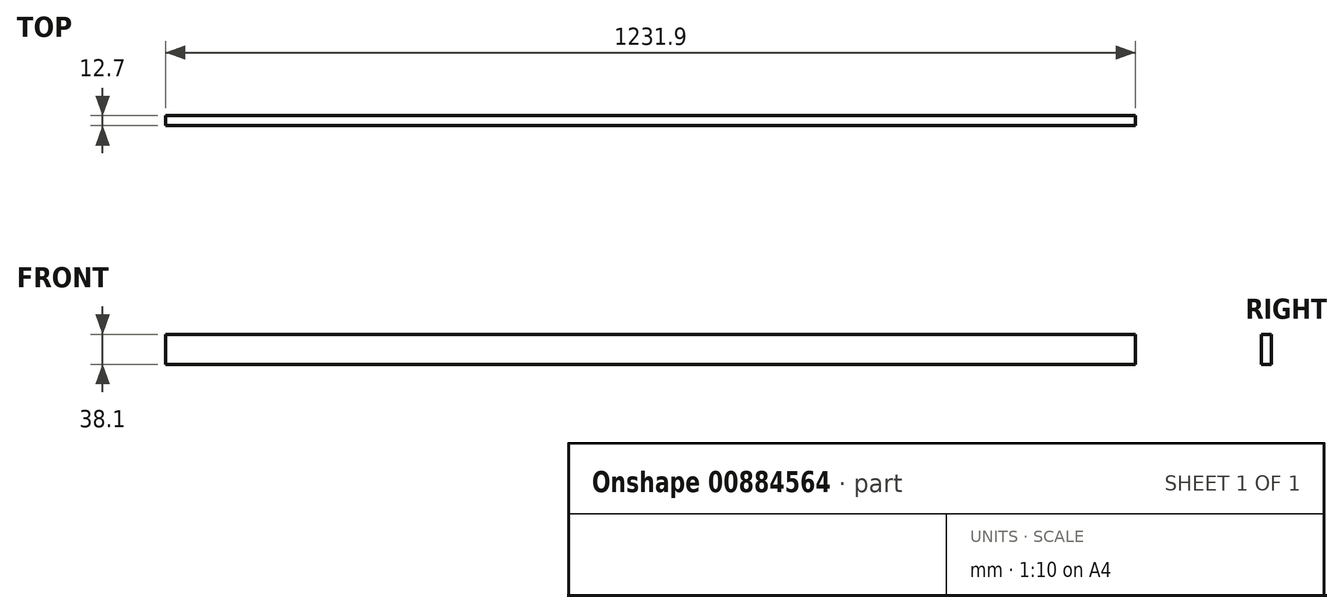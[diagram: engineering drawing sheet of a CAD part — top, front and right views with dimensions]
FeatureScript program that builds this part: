
annotation { "Feature Type Name" : "Feature", "Feature Type Description" : "" }
export const myFeature = defineFeature(function(context is Context, id is Id, definition is map)
    precondition{}
    {
        {
            var Q0;
            Q0=qCreatedBy(makeId("Right.planeOp"),FACE);
            var sketch = newSketch(context, id + "F0", { "sketchPlane" : qUnion([Q0])});
            skLineSegment(sketch, "E0.bottom", {"start": v(6.35, -19.05) * mm, "end": v(-6.35, -19.05) * mm});
            skLineSegment(sketch, "E0.top", {"start": v(6.35, 19.05) * mm, "end": v(-6.35, 19.05) * mm});
            skLineSegment(sketch, "E0.left", {"start": v(6.35, -19.05) * mm, "end": v(6.35, 19.05) * mm});
            skLineSegment(sketch, "E0.right", {"start": v(-6.35, -19.05) * mm, "end": v(-6.35, 19.05) * mm});
            skPoint(sketch, "E0.middle", {"position": v(0, 0) * mm});
            skSolve(sketch);
        }
        {
            var Q0;
            Q0=makeQuery(id+"F0.imprint","IMPRINT",FACE,{"disambiguationData":[TD([[makeQuery(id+"F0.imprint","IMPRINT",EDGE,{"derivedFrom":sQuery(id+"F0.wireOp",EDGE,"E0.bottom")}),-1.0]])]});
            extrude(context, id + "F1", {"entities" : qUnion([Q0]), "endBound" : BoundingType.SYMMETRIC, "depth" : 1231.9 * mm, "offsetDistance" : 25.4 * mm});
        }
    });
